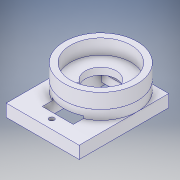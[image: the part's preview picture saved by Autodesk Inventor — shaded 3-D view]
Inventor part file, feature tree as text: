
AUTODESK INVENTOR PART (.ipt)
format: ipt  version: 2017 (Build 210142000, 142)  size: 202,752 bytes
history: native  units: in
note: dims shown in document units (in); Inventor stores cm internally (conversion verified against a paired STEP export)
features: extrude x6, sketch x6, projected_geometry x2, plane x1
ambient origin geometry x8: Origin, YZ Plane, XZ Plane, XY Plane, X Axis, Y Axis, Z Axis, Center Point
bodies: Solid1 (feature_tree)
feature tree (15):
  extrude  "Extrusion1"  Depth=1.4252in
  sketch  "Sketch2"  dims[d2=0.1969in d3=0.0in d4=0.689in]
  extrude  "Extrusion2"  Depth=0.1969in
  extrude  "Extrusion3"  Depth=0.2362in
  extrude  "Extrusion4"  Depth=0.9587in
  extrude  "Extrusion5"  Depth=0.1496in TaperAngle=0.0deg
  plane  "Work Plane1"
  extrude  "Extrusion6"  Depth=0.2362in TaperAngle=0.0deg
  sketch  "Sketch1"  dims[d0=1.1614in d1=1.4252in]
  sketch  "Sketch4"  dims[d5=0.2992in d6=0.2362in]
  sketch  "Sketch5"  dims[d7=0.4921in d8=0.9587in]
  projected_geometry  "Projected Loop2"
  sketch  "Sketch6"  dims[d9=1.1614in d10=0.1496in d11=0.0in]
  projected_geometry  "Projected Loop3"
  sketch  "Sketch7"  dims[d12=0.9646in d13=0.2362in d14=0.0in d15=0.2362in d16=0.0in d17=0.4943in d18=1.3031in d19=0.2362in d20=0.0in d21=-0.0591in d22=0.1788in d23=0.4943in d24=0.1788in d25=0.494in d26=0.082in d27=0.0in d28=0.082in d29=0.0in d30=0.0787in d31=0.0787in d32=0.2362in d33=0.0in]
